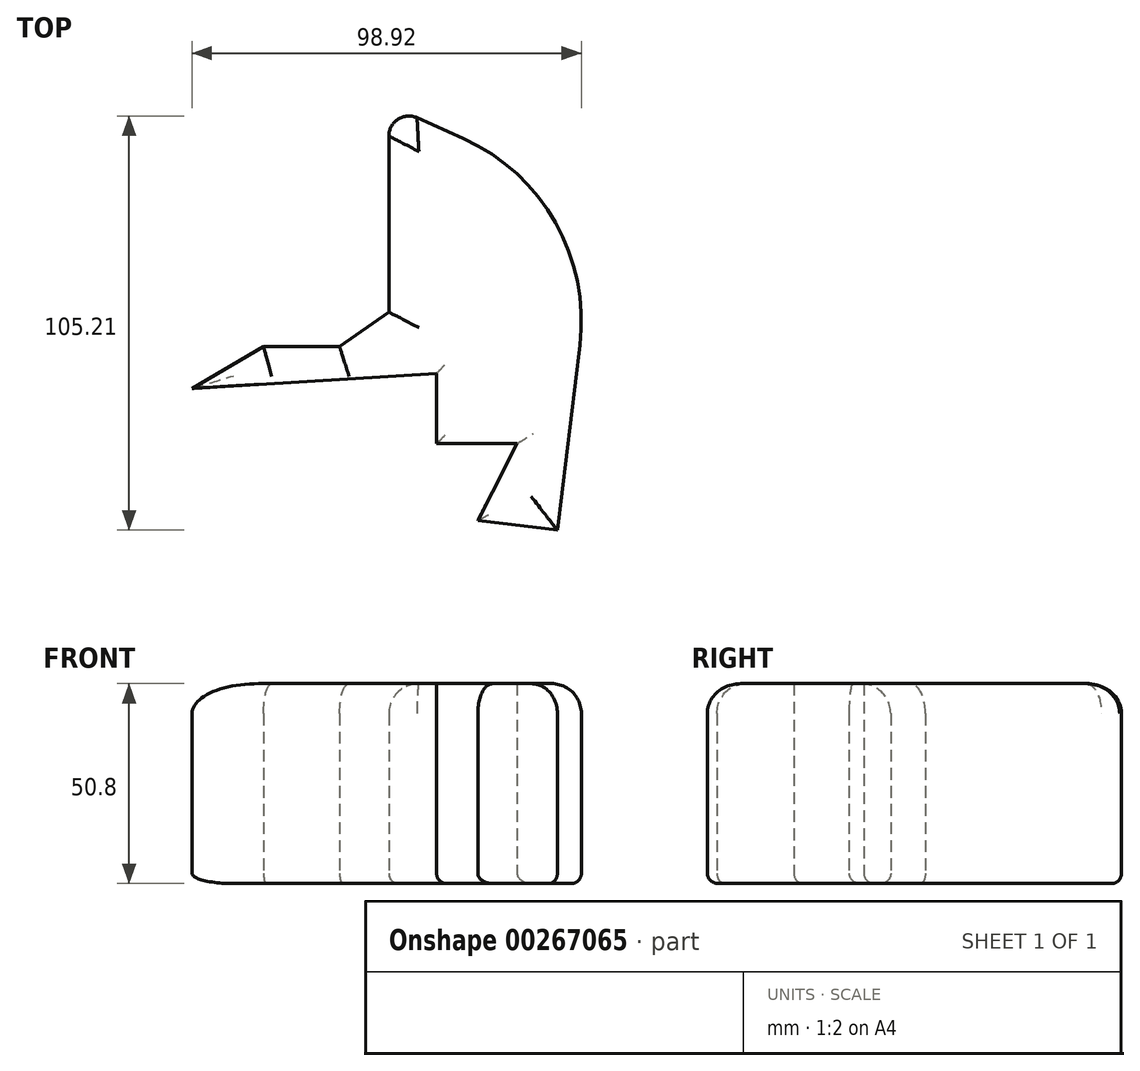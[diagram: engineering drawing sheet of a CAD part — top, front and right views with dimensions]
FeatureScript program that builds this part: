
annotation { "Feature Type Name" : "Feature", "Feature Type Description" : "" }
export const myFeature = defineFeature(function(context is Context, id is Id, definition is map)
    precondition{}
    {
        {
            var Q0;
            Q0=qCreatedBy(makeId("Top.planeOp"),FACE);
            var sketch = newSketch(context, id + "F0", { "sketchPlane" : qUnion([Q0])});
            skLineSegment(sketch, "E0", {"start": v(0, 0) * mm, "end": v(0, 52.58) * mm});
            skLineSegment(sketch, "E1", {"start": v(0, 52.58) * mm, "end": v(53.05, 28.71) * mm});
            skLineSegment(sketch, "E2", {"start": v(53.05, 28.71) * mm, "end": v(42.82, -55.4) * mm});
            skLineSegment(sketch, "E3", {"start": v(42.82, -55.4) * mm, "end": v(22.62, -52.94) * mm});
            skLineSegment(sketch, "E4", {"start": v(22.62, -52.94) * mm, "end": v(32.59, -33.42) * mm});
            skLineSegment(sketch, "E5", {"start": v(32.59, -33.42) * mm, "end": v(12.13, -33.42) * mm});
            skLineSegment(sketch, "E6", {"start": v(12.13, -33.42) * mm, "end": v(12.13, -15.62) * mm});
            skLineSegment(sketch, "E7", {"start": v(12.13, -15.62) * mm, "end": v(-50, -19.4) * mm});
            skLineSegment(sketch, "E8", {"start": v(-50, -19.4) * mm, "end": v(-31.82, -8.8) * mm});
            skLineSegment(sketch, "E9", {"start": v(-31.82, -8.8) * mm, "end": v(-12.5, -8.8) * mm});
            skLineSegment(sketch, "E10", {"start": v(-12.5, -8.8) * mm, "end": v(0, 0) * mm});
            skSolve(sketch);
        }
        {
            var Q0;
            Q0 = qSketchRegion(id + "F0", true);
            extrude(context, id + "F1", {"entities" : qUnion([Q0]), "depth" : 50.8 * mm});
        }
        {
            var Q0;
            Q0=makeQuery(id+"F1.opExtrude","CAP_EDGE",EDGE,{"disambiguationData":[OSD([sQuery(id+"F0.wireOp",EDGE,"E2")])],"isStart":false});
            var Q1;
            Q1=makeQuery(id+"F1.opExtrude","CAP_EDGE",EDGE,{"disambiguationData":[OSD([sQuery(id+"F0.wireOp",EDGE,"E3")])],"isStart":false});
            var Q2;
            Q2=makeQuery(id+"F1.opExtrude","CAP_EDGE",EDGE,{"disambiguationData":[OSD([sQuery(id+"F0.wireOp",EDGE,"E1")])],"isStart":false});
            var Q3;
            Q3=makeQuery(id+"F1.opExtrude","CAP_EDGE",EDGE,{"disambiguationData":[OSD([sQuery(id+"F0.wireOp",EDGE,"E0")])],"isStart":false});
            var Q4;
            Q4=makeQuery(id+"F1.opExtrude","CAP_EDGE",EDGE,{"disambiguationData":[OSD([sQuery(id+"F0.wireOp",EDGE,"E10")])],"isStart":false});
            var Q5;
            Q5=makeQuery(id+"F1.opExtrude","CAP_EDGE",EDGE,{"disambiguationData":[OSD([sQuery(id+"F0.wireOp",EDGE,"E9")])],"isStart":false});
            var Q6;
            Q6=makeQuery(id+"F1.opExtrude","CAP_EDGE",EDGE,{"disambiguationData":[OSD([sQuery(id+"F0.wireOp",EDGE,"E8")])],"isStart":false});
            fillet(context, id + "F2", {"entities" : qUnion([Q0, Q1, Q2, Q3, Q4, Q5, Q6]), "radius" : 7.62 * mm, "tangentPropagation" : true, "allowEdgeOverflow" : false});
        }
        {
            var Q0;
            Q0=makeQuery(id+"F1.opExtrude","SWEPT_EDGE",EDGE,{"disambiguationData":[OSD([sQuery(id+"F0.wireOp",EDGE,"E1"),sQuery(id+"F0.wireOp",EDGE,"E2")])]});
            fillet(context, id + "F3", {"entities" : qUnion([Q0]), "radius" : 50.8 * mm, "tangentPropagation" : true, "allowEdgeOverflow" : false});
        }
        {
            var Q0;
            Q0=makeQuery(id+"F1.opExtrude","SWEPT_EDGE",EDGE,{"disambiguationData":[OSD([sQuery(id+"F0.wireOp",EDGE,"E0"),sQuery(id+"F0.wireOp",EDGE,"E1")])]});
            fillet(context, id + "F4", {"entities" : qUnion([Q0]), "radius" : 5.08 * mm, "tangentPropagation" : true, "allowEdgeOverflow" : false});
        }
        {
            var Q0;
            Q0=makeQuery(id+"F1.opExtrude","CAP_FACE",FACE,{"disambiguationData":[OSD([sQuery(id+"F0.wireOp",EDGE,"E0"),sQuery(id+"F0.wireOp",EDGE,"E1"),sQuery(id+"F0.wireOp",EDGE,"E2"),sQuery(id+"F0.wireOp",EDGE,"E3"),sQuery(id+"F0.wireOp",EDGE,"E4"),sQuery(id+"F0.wireOp",EDGE,"E5"),sQuery(id+"F0.wireOp",EDGE,"E6"),sQuery(id+"F0.wireOp",EDGE,"E7"),sQuery(id+"F0.wireOp",EDGE,"E8"),sQuery(id+"F0.wireOp",EDGE,"E9"),sQuery(id+"F0.wireOp",EDGE,"E10")])],"isStart":true});
            fillet(context, id + "F5", {"entities" : qUnion([Q0]), "radius" : 2.54 * mm, "tangentPropagation" : true, "allowEdgeOverflow" : false});
        }
    });
